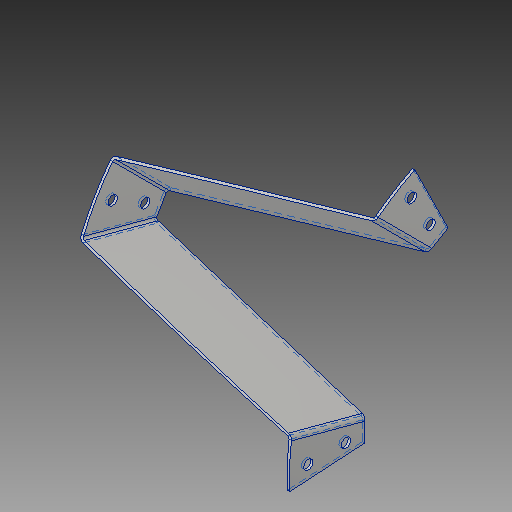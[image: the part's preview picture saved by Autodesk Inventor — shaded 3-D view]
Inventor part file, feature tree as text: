
AUTODESK INVENTOR PART (.ipt)
format: ipt  version: 2019 (Build 230136000, 136)  size: 286,208 bytes
history: native  units: in
note: dims shown in document units (in); Inventor stores cm internally (conversion verified against a paired STEP export)
features: sheet_metal_op x5, sketch x3, other x3, plane x2, extrude x1
ambient origin geometry x8: Origin, YZ Plane, XZ Plane, XY Plane, X Axis, Y Axis, Z Axis, Center Point
bodies: Solid1 (feature_tree)
feature tree (14):
  plane  "Work Plane1"
  plane  "Work Plane2"
  sketch  "Sketch1"  dims[d0=3.0in d1=-3.0in d2=12.0in]
  sketch  "Sketch2"  dims[d3=0.25in]
  sheet_metal_op  "Face1"
  sheet_metal_op  "Face2"
  sheet_metal_op  "Bend2"
  sheet_metal_op  "Bend3"
  extrude  "Extrusion1"  Depth=3.0in
  other  "Plate1"
  other  "Plate2"
  sheet_metal_op  "Bend1"
  sketch  "Sketch3"  dims[d4=1.0in d5=0.5in d6=4.7244in d8=360.0deg d10=0.5in d11=0.5in d12=0.0625in d13=0.0625in d14=0.0625in d15=0.0312in d16=0.125in d17=0.0625in d18=0.0625in d19=0.0312in d20=0.125in d21=0.0625in d22=0.0625in d23=0.0625in d24=0.0312in d25=0.125in d26=0.0625in d27=0.0625in d28=12.0in d29=20.0in d30=0.0in d31=0.0in d32=0.0625in]
  other  "Definition1"
